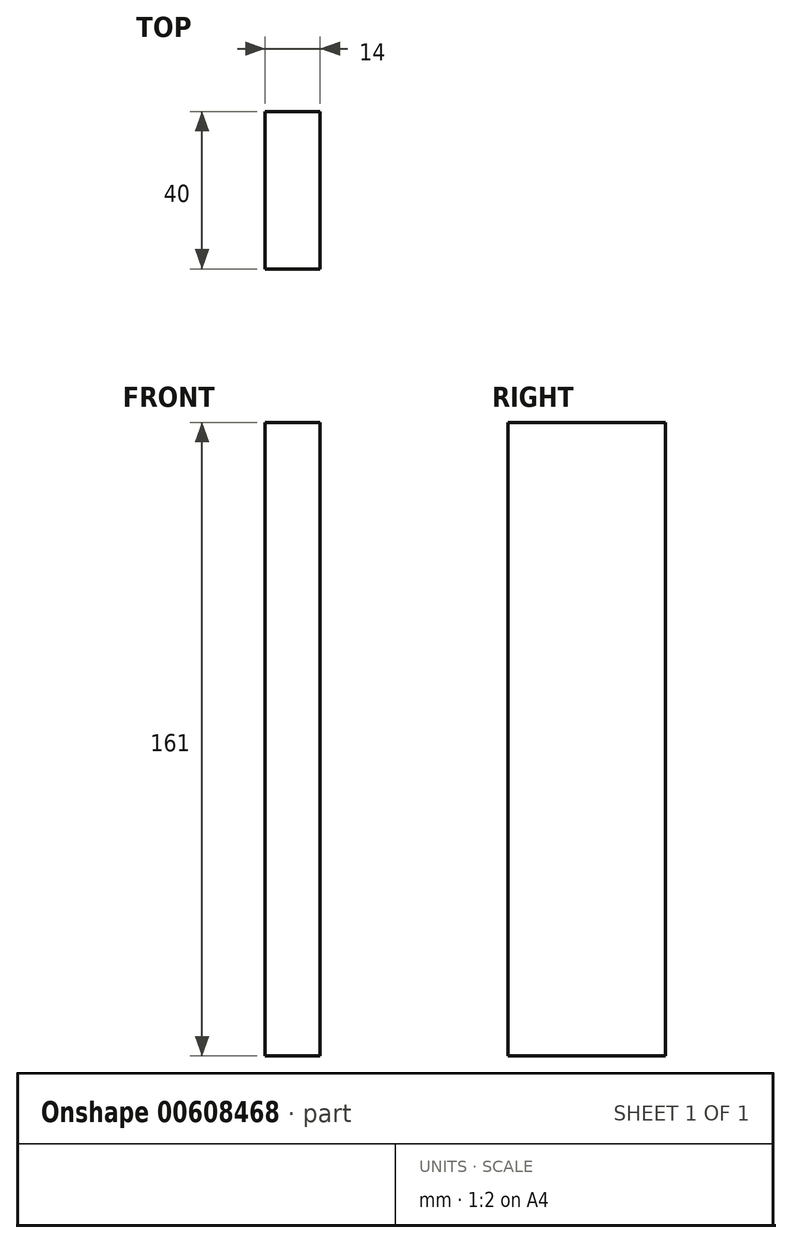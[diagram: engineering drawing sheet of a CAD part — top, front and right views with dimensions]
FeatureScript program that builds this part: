
annotation { "Feature Type Name" : "Feature", "Feature Type Description" : "" }
export const myFeature = defineFeature(function(context is Context, id is Id, definition is map)
    precondition{}
    {
        {
            var Q0;
            Q0=qCreatedBy(makeId("Right.planeOp"),FACE);
            var sketch = newSketch(context, id + "F0", { "sketchPlane" : qUnion([Q0])});
            skLineSegment(sketch, "E0.bottom", {"start": v(0, 0) * mm, "end": v(40, 0) * mm});
            skLineSegment(sketch, "E0.top", {"start": v(0, -161) * mm, "end": v(40, -161) * mm});
            skLineSegment(sketch, "E0.left", {"start": v(0, 0) * mm, "end": v(0, -161) * mm});
            skLineSegment(sketch, "E0.right", {"start": v(40, 0) * mm, "end": v(40, -161) * mm});
            skSolve(sketch);
        }
        {
            var Q0;
            Q0=makeQuery(id+"F0.imprint","IMPRINT",FACE,{"disambiguationData":[TD([[makeQuery(id+"F0.imprint","IMPRINT",EDGE,{"derivedFrom":sQuery(id+"F0.wireOp",EDGE,"E0.bottom")}),-1.0]])]});
            extrude(context, id + "F1", {"entities" : qUnion([Q0]), "depth" : 14 * mm, "offsetDistance" : 25 * mm});
        }
    });
